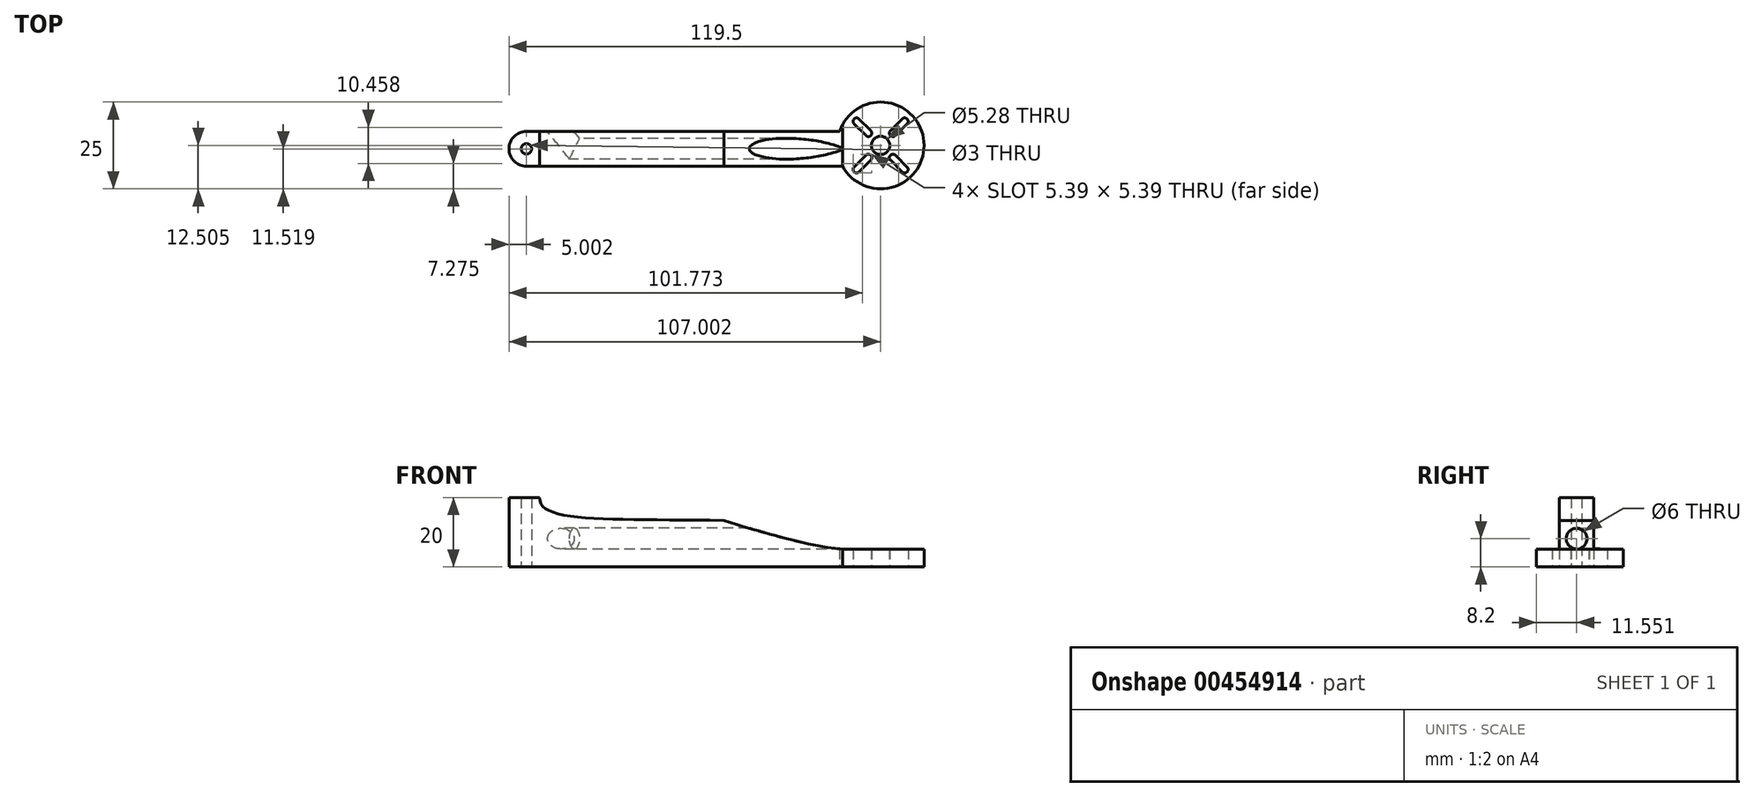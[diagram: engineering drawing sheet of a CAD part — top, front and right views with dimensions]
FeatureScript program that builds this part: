
annotation { "Feature Type Name" : "Feature", "Feature Type Description" : "" }
export const myFeature = defineFeature(function(context is Context, id is Id, definition is map)
    precondition{}
    {
        {
            var Q0;
            Q0=qCreatedBy(makeId("Top.planeOp"),FACE);
            var sketch = newSketch(context, id + "F0", { "sketchPlane" : qUnion([Q0])});
            skLineSegment(sketch, "E0", {"start": v(-139.16, 59.15) * mm, "end": v(-37.16, 59.15) * mm, "construction": true});
            skArc(sketch, "E1", {"start": v(-48.13, 53.17) * mm, "mid": v(-24.7, 60.23) * mm, "end": v(-49, 63.17) * mm});
            skLineSegment(sketch, "E2", {"start": v(-139.16, 63.17) * mm, "end": v(-49, 63.17) * mm});
            skLineSegment(sketch, "E3", {"start": v(-139.16, 53.17) * mm, "end": v(-48.13, 53.17) * mm});
            skCircle(sketch, "E4", {"center": v(-37.16, 59.15) * mm, "radius": 2.64 * mm});
            skArc(sketch, "E5.0.startCap", {"start": v(-44.79, 65.37) * mm, "mid": v(-44.79, 66.78) * mm, "end": v(-43.37, 66.78) * mm});
            skArc(sketch, "E5.0.endCap", {"start": v(-39.99, 63.4) * mm, "mid": v(-39.99, 61.98) * mm, "end": v(-41.4, 61.98) * mm});
            skLineSegment(sketch, "E5.0.left", {"start": v(-43.37, 66.78) * mm, "end": v(-39.99, 63.4) * mm});
            skLineSegment(sketch, "E5.0.right", {"start": v(-44.79, 65.37) * mm, "end": v(-41.4, 61.98) * mm});
            skLineSegment(sketch, "E6", {"start": v(-37.16, 59.15) * mm, "end": v(-37.16, 66.76) * mm, "construction": true});
            skArc(sketch, "E7.MirrorCS", {"start": v(-29.53, 65.37) * mm, "mid": v(-29.53, 66.78) * mm, "end": v(-30.94, 66.78) * mm});
            skArc(sketch, "E8.MirrorCS", {"start": v(-34.33, 63.4) * mm, "mid": v(-34.33, 61.98) * mm, "end": v(-32.92, 61.98) * mm});
            skLineSegment(sketch, "E9.MirrorCS", {"start": v(-29.53, 65.37) * mm, "end": v(-32.92, 61.98) * mm});
            skLineSegment(sketch, "E10.MirrorCS", {"start": v(-30.94, 66.78) * mm, "end": v(-34.33, 63.4) * mm});
            skLineSegment(sketch, "E11.MirrorCS", {"start": v(-30.94, 51.52) * mm, "end": v(-34.33, 54.91) * mm});
            skArc(sketch, "E12.MirrorCS", {"start": v(-29.53, 52.94) * mm, "mid": v(-29.53, 51.52) * mm, "end": v(-30.94, 51.52) * mm});
            skLineSegment(sketch, "E13.MirrorCS", {"start": v(-29.53, 52.94) * mm, "end": v(-32.92, 56.33) * mm});
            skArc(sketch, "E14.MirrorCS", {"start": v(-34.33, 54.91) * mm, "mid": v(-34.33, 56.33) * mm, "end": v(-32.92, 56.33) * mm});
            skLineSegment(sketch, "E15.MirrorCS", {"start": v(-44.79, 52.94) * mm, "end": v(-41.4, 56.33) * mm});
            skLineSegment(sketch, "E16.MirrorCS", {"start": v(-43.37, 51.52) * mm, "end": v(-39.99, 54.91) * mm});
            skArc(sketch, "E17.MirrorCS", {"start": v(-39.99, 54.91) * mm, "mid": v(-39.99, 56.33) * mm, "end": v(-41.4, 56.33) * mm});
            skArc(sketch, "E18.MirrorCS", {"start": v(-44.79, 52.94) * mm, "mid": v(-44.79, 51.52) * mm, "end": v(-43.37, 51.52) * mm});
            skLineSegment(sketch, "E19", {"start": v(-37.16, 59.15) * mm, "end": v(-44.76, 66.76) * mm, "construction": true});
            skLineSegment(sketch, "E20", {"start": v(-139.16, 53.17) * mm, "end": v(-139.16, 63.17) * mm, "construction": true});
            skPoint(sketch, "E21", {"position": v(-139.16, 58.17) * mm});
            skArc(sketch, "E22", {"start": v(-139.16, 53.17) * mm, "mid": v(-144.16, 58.17) * mm, "end": v(-139.16, 63.17) * mm});
            skCircle(sketch, "E23", {"center": v(-139.16, 58.17) * mm, "radius": 1.5 * mm});
            skSolve(sketch);
        }
        {
            var Q0;
            Q0=qSketchRegion(id+"F0",true);
            extrude(context, id + "F1", {"entities" : qUnion([Q0]), "depth" : 20 * mm});
        }
        {
            var Q0;
            Q0=makeQuery(id+"F1.opExtrude","SWEPT_FACE",FACE,{"disambiguationData":[OSD([sQuery(id+"F0.wireOp",EDGE,"E3")])]});
            var sketch = newSketch(context, id + "F2", { "sketchPlane" : qUnion([Q0])});
            skFitSpline(sketch, "E24", {"points": [v(-48.13, 5.2) * mm, v(-101.02, 20) * mm], "startDerivative": vector(-37.65, 1.6) * mm, "endDerivative": vector(-23.18, 9.57) * mm});
            skLineSegment(sketch, "E25", {"start": v(-48.13, 5.2) * mm, "end": v(66.1, 5.2) * mm});
            skLineSegment(sketch, "E26", {"start": v(66.1, 5.2) * mm, "end": v(64.34, 23.02) * mm});
            skLineSegment(sketch, "E27", {"start": v(64.34, 23.02) * mm, "end": v(-14.17, 23.97) * mm});
            skLineSegment(sketch, "E28", {"start": v(-14.17, 23.97) * mm, "end": v(-21.08, 20) * mm});
            skLineSegment(sketch, "E29", {"start": v(-48.13, 13.43) * mm, "end": v(-82.25, 13.43) * mm});
            skLineSegment(sketch, "E30", {"start": v(-48.13, 13.43) * mm, "end": v(-48.13, 24.34) * mm});
            skLineSegment(sketch, "E31", {"start": v(-48.13, 24.34) * mm, "end": v(-21.08, 20) * mm});
            skSolve(sketch);
        }
        {
            var Q0;
            Q0=qSketchRegion(id+"F2",true);
            extrude(context, id + "F3", {"entities" : qUnion([Q0]), "operationType" : NewBodyOperationType.REMOVE, "oppositeDirection" : true, "depth" : 25 * mm, "hasSecondDirection" : true, "secondDirectionOppositeDirection" : false, "secondDirectionDepth" : 25 * mm});
        }
        {
            var Q0;
            Q0=makeQuery(id+"F3.boolean.opBoolean","COPY",FACE,{"derivedFrom":makeQuery(id+"F3.opExtrude","SWEPT_FACE",FACE,{"disambiguationData":[OSD([sQuery(id+"F2.wireOp",EDGE,"E25")])]})});
            var sketch = newSketch(context, id + "F4", { "sketchPlane" : qUnion([Q0])});
            skLineSegment(sketch, "E32", {"start": v(-86.71, 58.17) * mm, "end": v(-61.2, 58.17) * mm});
            skLineSegment(sketch, "E33", {"start": v(-86.71, 58.17) * mm, "end": v(-125.32, 58.17) * mm});
            skLineSegment(sketch, "E34", {"start": v(-125.32, 58.17) * mm, "end": v(-138.96, 75.4) * mm});
            skSolve(sketch);
        }
        {
            var Q0;
            Q0=makeQuery(id+"F3.boolean.opBoolean","COPY",EDGE,{"derivedFrom":makeQuery(id+"F3.opExtrude","SWEPT_EDGE",EDGE,{"disambiguationData":[OSD([sQuery(id+"F0.wireOp",EDGE,"E1"),sQuery(id+"F0.wireOp",EDGE,"E3"),sQuery(id+"F2.wireOp",EDGE,"E24"),sQuery(id+"F2.wireOp",EDGE,"E25")])]})});
            cPlane(context, id + "F5", {"entities" : qUnion([Q0]), "cplaneType" : CPlaneType.LINE_ANGLE, "offset" : 25 * mm, "angle" : 90 * degree, "width" : 150 * mm, "height" : 150 * mm});
        }
        {
            var Q0;
            Q0=qCreatedBy(id+"F5.planeOp",FACE);
            var sketch = newSketch(context, id + "F6", { "sketchPlane" : qUnion([Q0])});
            skLineSegment(sketch, "E35.0", {"start": v(65.14, 5.2) * mm, "end": v(53.17, 5.2) * mm, "construction": true});
            skCircle(sketch, "E36", {"center": v(58.2, 8.2) * mm, "radius": 3 * mm});
            skSolve(sketch);
        }
        {
            var Q0;
            Q0=qSketchRegion(id+"F6",true);
            var Q1;
            Q1=qConstructionFilter(qBodyType(qCreatedBy(id+"F4",EDGE),BodyType.WIRE),ConstructionObject.NO);
            sweep(context, id + "F7", {"operationType" : NewBodyOperationType.REMOVE, "profiles" : qUnion([Q0]), "path" : qUnion([Q1])});
        }
        {
            var Q0;
            Q0=makeQuery(id+"F1.opExtrude","SWEPT_FACE",FACE,{"disambiguationData":[OSD([sQuery(id+"F0.wireOp",EDGE,"E3")])]});
            var sketch = newSketch(context, id + "F8", { "sketchPlane" : qUnion([Q0])});
            skPoint(sketch, "E37.0", {"position": v(-82.25, 13.43) * mm});
            skFitSpline(sketch, "E38", {"points": [v(-82.25, 13.43) * mm, v(-135.35, 20) * mm], "startDerivative": vector(-96, 1.58) * mm, "endDerivative": vector(1.3, 22.57) * mm});
            skLineSegment(sketch, "E39", {"start": v(-82.25, 13.43) * mm, "end": v(-32.97, 11.71) * mm});
            skLineSegment(sketch, "E40", {"start": v(-32.97, 11.71) * mm, "end": v(-32.97, 37.38) * mm});
            skLineSegment(sketch, "E41", {"start": v(-32.97, 37.38) * mm, "end": v(-135.35, 20) * mm});
            skSolve(sketch);
        }
        {
            var Q0;
            Q0 = qSketchRegion(id + "F8", true);
            extrude(context, id + "F9", {"entities" : qUnion([Q0]), "operationType" : NewBodyOperationType.REMOVE, "oppositeDirection" : true, "depth" : 25 * mm});
        }
    });
